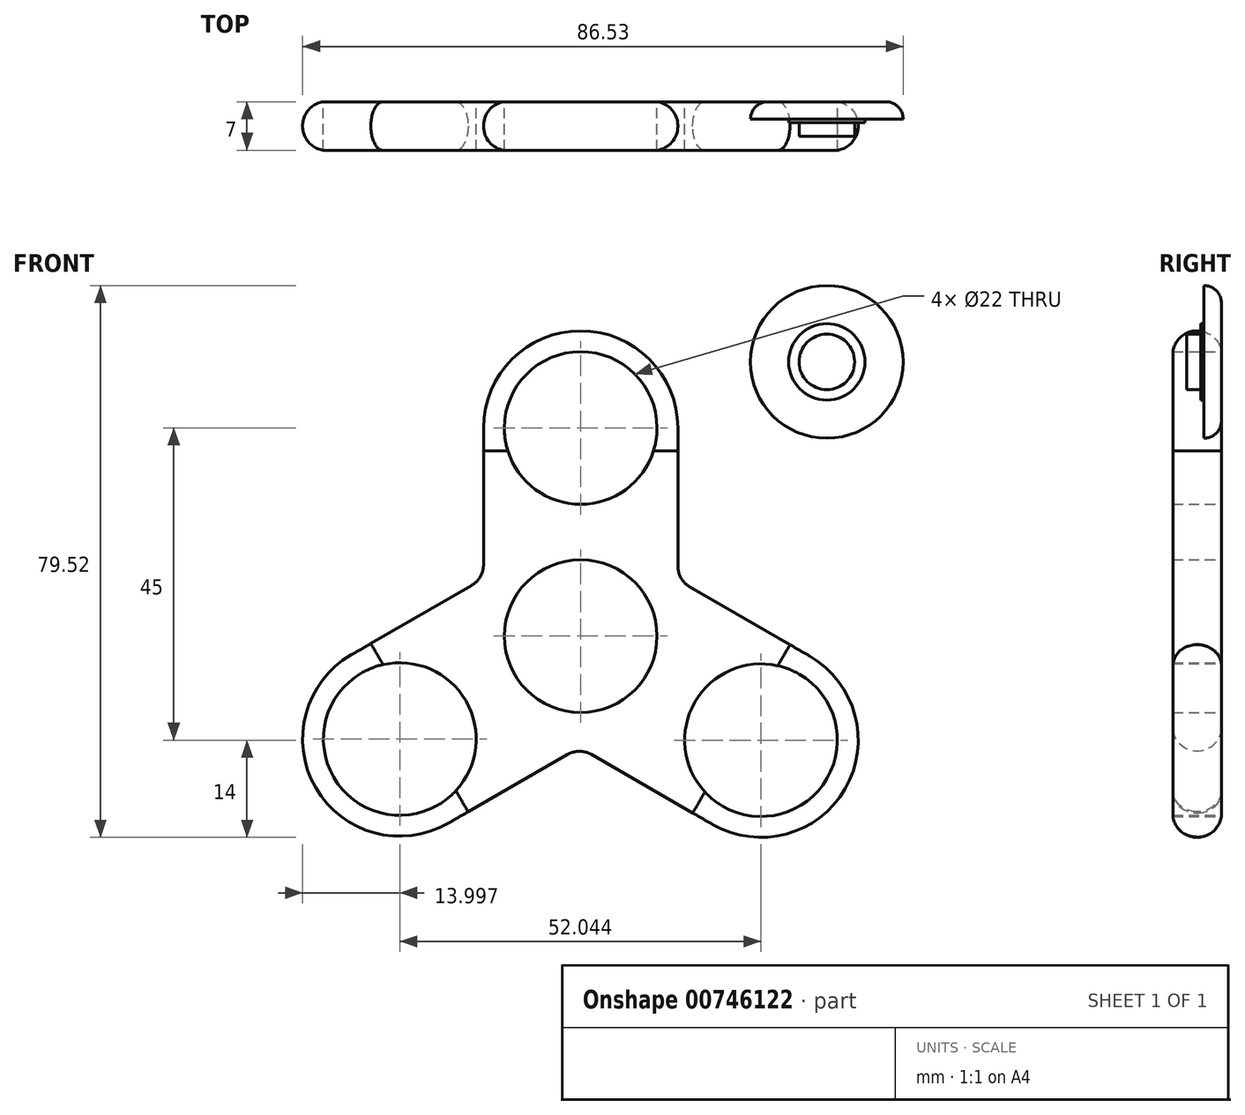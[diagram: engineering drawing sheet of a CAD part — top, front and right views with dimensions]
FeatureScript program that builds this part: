
annotation { "Feature Type Name" : "Feature", "Feature Type Description" : "" }
export const myFeature = defineFeature(function(context is Context, id is Id, definition is map)
    precondition{}
    {
        {
            var Q0;
            Q0=qCreatedBy(makeId("Front.planeOp"),FACE);
            var sketch = newSketch(context, id + "F0", { "sketchPlane" : qUnion([Q0])});
            skLineSegment(sketch, "E0.left", {"start": v(-14, -6.7) * mm, "end": v(-14, 15) * mm});
            skLineSegment(sketch, "E0.right", {"start": v(14, -6.92) * mm, "end": v(14, 15) * mm});
            skPoint(sketch, "E0.middle", {"position": v(0, 0) * mm});
            skArc(sketch, "E1", {"start": v(14, 15) * mm, "mid": v(0, 29) * mm, "end": v(-14, 15) * mm});
            skLineSegment(sketch, "E2.right", {"start": v(-0.18, -31.06) * mm, "end": v(18.98, -42.12) * mm});
            skArc(sketch, "E3", {"start": v(18.98, -42.12) * mm, "mid": v(38.1, -37) * mm, "end": v(32.98, -17.88) * mm});
            skLineSegment(sketch, "E4.right", {"start": v(-14, -6.7) * mm, "end": v(-33.06, -17.71) * mm});
            skArc(sketch, "E5", {"start": v(-33.06, -17.71) * mm, "mid": v(-38.19, -36.84) * mm, "end": v(-19.06, -41.96) * mm});
            skLineSegment(sketch, "E6.trimOffspring", {"start": v(-0.18, -31.06) * mm, "end": v(-19.06, -41.96) * mm});
            skLineSegment(sketch, "E7.trimOffspring", {"start": v(14, -6.92) * mm, "end": v(32.98, -17.88) * mm});
            skCircle(sketch, "E8", {"center": v(0, -15) * mm, "radius": 11 * mm});
            skCircle(sketch, "E9", {"center": v(-26.06, -29.84) * mm, "radius": 11 * mm});
            skCircle(sketch, "E10", {"center": v(25.98, -30) * mm, "radius": 11 * mm});
            skCircle(sketch, "E11", {"center": v(0, 15) * mm, "radius": 11 * mm});
            skSolve(sketch);
        }
        {
            var Q0;
            Q0=makeQuery(id+"F0.imprint","IMPRINT",FACE,{"disambiguationData":[TD([[makeQuery(id+"F0.imprint","IMPRINT",EDGE,{"derivedFrom":sQuery(id+"F0.wireOp",EDGE,"E0.left")}),-1.0]])]});
            extrude(context, id + "F1", {"entities" : qUnion([Q0]), "depth" : 7 * mm, "offsetDistance" : 25 * mm});
        }
        {
            var Q0;
            Q0=qCreatedBy(makeId("Front.planeOp"),FACE);
            var sketch = newSketch(context, id + "F2", { "sketchPlane" : qUnion([Q0])});
            skCircle(sketch, "E12", {"center": v(35.47, 24.52) * mm, "radius": 11 * mm});
            skCircle(sketch, "E13", {"center": v(35.47, 24.52) * mm, "radius": 5.5 * mm});
            skCircle(sketch, "E14", {"center": v(35.47, 24.52) * mm, "radius": 4 * mm});
            skSolve(sketch);
        }
        {
            var Q0;
            Q0=makeQuery(id+"F2.imprint","IMPRINT",FACE,{"disambiguationData":[TD([[makeQuery(id+"F2.imprint","IMPRINT",EDGE,{"derivedFrom":sQuery(id+"F2.wireOp",EDGE,"E12")}),1.0]])]});
            extrude(context, id + "F3", {"entities" : qUnion([Q0]), "depth" : 2.5 * mm, "offsetDistance" : 25 * mm});
        }
        {
            var Q0;
            Q0=makeQuery(id+"F2.imprint","IMPRINT",FACE,{"disambiguationData":[TD([[makeQuery(id+"F2.imprint","IMPRINT",EDGE,{"derivedFrom":sQuery(id+"F2.wireOp",EDGE,"E13")}),1.0]])]});
            extrude(context, id + "F4", {"entities" : qUnion([Q0]), "operationType" : NewBodyOperationType.ADD, "depth" : 3 * mm, "offsetDistance" : 25 * mm});
        }
        {
            var Q0;
            Q0=makeQuery(id+"F2.imprint","IMPRINT",FACE,{"disambiguationData":[TD([[makeQuery(id+"F2.imprint","IMPRINT",EDGE,{"derivedFrom":sQuery(id+"F2.wireOp",EDGE,"E14")}),1.0]])]});
            extrude(context, id + "F5", {"entities" : qUnion([Q0]), "operationType" : NewBodyOperationType.ADD, "depth" : 5 * mm, "offsetDistance" : 25 * mm});
        }
        {
            var Q0;
            Q0=makeQuery(id+"F1.opExtrude","SWEPT_FACE",FACE,{"disambiguationData":[OSD([sQuery(id+"F0.wireOp",EDGE,"E0.left")])]});
            var Q1;
            Q1=makeQuery(id+"F1.opExtrude","SWEPT_FACE",FACE,{"disambiguationData":[OSD([sQuery(id+"F0.wireOp",EDGE,"E4.right")])]});
            var Q2;
            Q2=makeQuery(id+"F1.opExtrude","SWEPT_FACE",FACE,{"disambiguationData":[OSD([sQuery(id+"F0.wireOp",EDGE,"E5")])]});
            var Q3;
            Q3=makeQuery(id+"F1.opExtrude","SWEPT_FACE",FACE,{"disambiguationData":[OSD([sQuery(id+"F0.wireOp",EDGE,"E1")])]});
            var Q4;
            Q4=makeQuery(id+"F1.opExtrude","SWEPT_FACE",FACE,{"disambiguationData":[OSD([sQuery(id+"F0.wireOp",EDGE,"E6.trimOffspring")])]});
            var Q5;
            Q5=makeQuery(id+"F1.opExtrude","SWEPT_FACE",FACE,{"disambiguationData":[OSD([sQuery(id+"F0.wireOp",EDGE,"E3")])]});
            var Q6;
            Q6=makeQuery(id+"F1.opExtrude","SWEPT_FACE",FACE,{"disambiguationData":[OSD([sQuery(id+"F0.wireOp",EDGE,"E2.right")])]});
            var Q7;
            Q7=makeQuery(id+"F1.opExtrude","SWEPT_FACE",FACE,{"disambiguationData":[OSD([sQuery(id+"F0.wireOp",EDGE,"E7.trimOffspring")])]});
            var Q8;
            Q8=makeQuery(id+"F1.opExtrude","SWEPT_FACE",FACE,{"disambiguationData":[OSD([sQuery(id+"F0.wireOp",EDGE,"E0.right")])]});
            fillet(context, id + "F6", {"entities" : qUnion([Q0, Q1, Q2, Q3, Q4, Q5, Q6, Q7, Q8]), "radius" : 3.5 * mm, "tangentPropagation" : true, "allowEdgeOverflow" : false});
        }
        {
            var Q0;
            Q0=makeQuery(id+"F3.opExtrude","CAP_EDGE",EDGE,{"disambiguationData":[OSD([sQuery(id+"F2.wireOp",EDGE,"E12")])],"isStart":true});
            fillet(context, id + "F7", {"entities" : qUnion([Q0]), "radius" : 2.5 * mm, "tangentPropagation" : true, "allowEdgeOverflow" : false});
        }
    });
